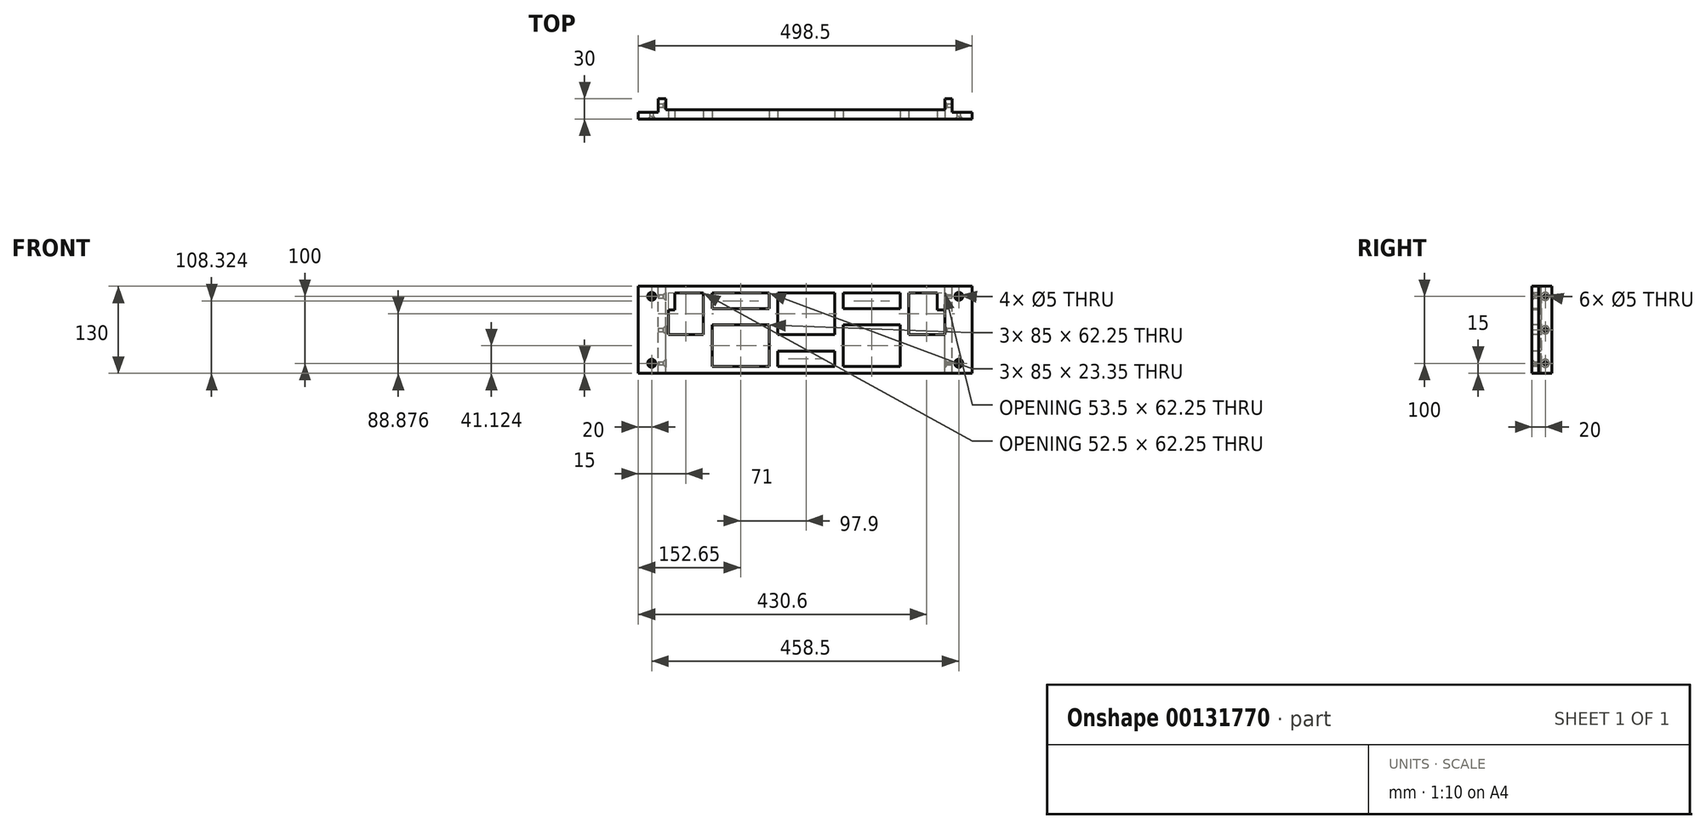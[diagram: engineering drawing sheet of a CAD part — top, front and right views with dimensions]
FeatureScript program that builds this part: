
annotation { "Feature Type Name" : "Feature", "Feature Type Description" : "" }
export const myFeature = defineFeature(function(context is Context, id is Id, definition is map)
    precondition{}
    {
        {
            var Q0;
            Q0=qCreatedBy(makeId("Front.planeOp"),FACE);
            var sketch = newSketch(context, id + "F0", { "sketchPlane" : qUnion([Q0])});
            skLineSegment(sketch, "E0.bottom", {"start": v(0, 0) * mm, "end": v(438.5, 0) * mm});
            skLineSegment(sketch, "E0.top", {"start": v(0, 130) * mm, "end": v(438.5, 130) * mm});
            skLineSegment(sketch, "E0.left", {"start": v(0, 0) * mm, "end": v(0, 130) * mm});
            skLineSegment(sketch, "E0.right", {"start": v(438.5, 0) * mm, "end": v(438.5, 130) * mm});
            skSolve(sketch);
        }
        {
            var Q0;
            Q0=makeQuery(id+"F0.imprint","IMPRINT",FACE,{"disambiguationData":[TD([[makeQuery(id+"F0.imprint","IMPRINT",EDGE,{"derivedFrom":sQuery(id+"F0.wireOp",EDGE,"E0.bottom")}),1.0]])]});
            extrude(context, id + "F1", {"entities" : qUnion([Q0]), "depth" : 14 * mm});
        }
        {
            var Q0;
            Q0=makeQuery(id+"F1.opExtrude","SWEPT_FACE",FACE,{"disambiguationData":[OSD([sQuery(id+"F0.wireOp",EDGE,"E0.top")])]});
            var sketch = newSketch(context, id + "F2", { "sketchPlane" : qUnion([Q0])});
            skLineSegment(sketch, "E1", {"start": v(0, -14) * mm, "end": v(-30, -14) * mm});
            skLineSegment(sketch, "E2", {"start": v(-30, -14) * mm, "end": v(-30, -4) * mm});
            skLineSegment(sketch, "E3", {"start": v(-30, -4) * mm, "end": v(0, -4) * mm});
            skLineSegment(sketch, "E4", {"start": v(0, -4) * mm, "end": v(0, -14) * mm});
            skLineSegment(sketch, "E5.bottom", {"start": v(438.5, -14) * mm, "end": v(468.5, -14) * mm});
            skLineSegment(sketch, "E5.top", {"start": v(438.5, -4) * mm, "end": v(468.5, -4) * mm});
            skLineSegment(sketch, "E5.left", {"start": v(438.5, -14) * mm, "end": v(438.5, -4) * mm});
            skLineSegment(sketch, "E6", {"start": v(468.5, -4) * mm, "end": v(468.5, -14) * mm});
            skSolve(sketch);
        }
        {
            var Q0;
            Q0=makeQuery(id+"F2.imprint","IMPRINT",FACE,{"disambiguationData":[TD([[makeQuery(id+"F2.imprint","IMPRINT",EDGE,{"derivedFrom":sQuery(id+"F2.wireOp",EDGE,"E5.bottom")}),1.0]])]});
            var Q1;
            Q1=makeQuery(id+"F2.imprint","IMPRINT",FACE,{"disambiguationData":[TD([[makeQuery(id+"F2.imprint","IMPRINT",EDGE,{"derivedFrom":sQuery(id+"F2.wireOp",EDGE,"E1")}),-1.0]])]});
            var Q2;
            Q2=makeQuery(id+"F2.imprint","IMPRINT",FACE,{"disambiguationData":[TD([[makeQuery(id+"F2.imprint","IMPRINT",EDGE,{"derivedFrom":sQuery(id+"F2.wireOp",EDGE,"RW2Kzl6v-dZsG-AqaK-MO7M-Wq128sQEg4HD.bottom")}),-1.0]])]});
            var Q3;
            Q3=makeQuery(id+"F1.opExtrude","SWEPT_FACE",FACE,{"disambiguationData":[OSD([sQuery(id+"F0.wireOp",EDGE,"E0.bottom")])]});
            extrude(context, id + "F3", {"entities" : qUnion([Q0, Q1, Q2]), "operationType" : NewBodyOperationType.ADD, "endBound" : BoundingType.UP_TO_SURFACE, "oppositeDirection" : true, "endBoundEntityFace" : qUnion([Q3]), "depth" : 25 * mm});
        }
        {
            var Q0;
            Q0=makeQuery(id+"F3.boolean.opBoolean","MERGE",FACE,{"derivedFrom":[makeQuery(id+"F1.opExtrude","SWEPT_FACE",FACE,{"disambiguationData":[OSD([sQuery(id+"F0.wireOp",EDGE,"E0.top")])]}),makeQuery(id+"F3.opExtrude","CAP_FACE",FACE,{"disambiguationData":[OSD([sQuery(id+"F2.wireOp",EDGE,"E1"),sQuery(id+"F2.wireOp",EDGE,"E2"),sQuery(id+"F2.wireOp",EDGE,"E3"),sQuery(id+"F2.wireOp",EDGE,"E4")])],"isStart":true}),makeQuery(id+"F3.opExtrude","CAP_FACE",FACE,{"disambiguationData":[OSD([sQuery(id+"F2.wireOp",EDGE,"E5.bottom"),sQuery(id+"F2.wireOp",EDGE,"E5.top"),sQuery(id+"F2.wireOp",EDGE,"E5.left"),sQuery(id+"F2.wireOp",EDGE,"E5.right")])],"isStart":true})]});
            var sketch = newSketch(context, id + "F4", { "sketchPlane" : qUnion([Q0])});
            skLineSegment(sketch, "E7", {"start": v(0, 0) * mm, "end": v(0, 16) * mm});
            skLineSegment(sketch, "E8", {"start": v(0, 16) * mm, "end": v(11, 16) * mm});
            skLineSegment(sketch, "E9", {"start": v(11, 16) * mm, "end": v(11, 0) * mm});
            skLineSegment(sketch, "E10", {"start": v(11, 0) * mm, "end": v(0, 0) * mm});
            skLineSegment(sketch, "E11.bottom", {"start": v(438.5, 0) * mm, "end": v(427.5, 0) * mm});
            skLineSegment(sketch, "E11.top", {"start": v(438.5, 16) * mm, "end": v(427.5, 16) * mm});
            skLineSegment(sketch, "E11.left", {"start": v(438.5, 0) * mm, "end": v(438.5, 16) * mm});
            skLineSegment(sketch, "E11.right", {"start": v(427.5, 0) * mm, "end": v(427.5, 16) * mm});
            skSolve(sketch);
        }
        {
            var Q0;
            Q0=makeQuery(id+"F4.imprint","IMPRINT",FACE,{"disambiguationData":[TD([[makeQuery(id+"F4.imprint","IMPRINT",EDGE,{"derivedFrom":sQuery(id+"F4.wireOp",EDGE,"g1681GE8-kr8q-vAWY-LNZA-GesWc0OhcODc.bottom")}),1.0]])]});
            var Q1;
            Q1=makeQuery(id+"F4.imprint","IMPRINT",FACE,{"disambiguationData":[TD([[makeQuery(id+"F4.imprint","IMPRINT",EDGE,{"derivedFrom":sQuery(id+"F4.wireOp",EDGE,"E7")}),-1.0]])]});
            var Q2;
            Q2=makeQuery(id+"F4.imprint","IMPRINT",FACE,{"disambiguationData":[TD([[makeQuery(id+"F4.imprint","IMPRINT",EDGE,{"derivedFrom":sQuery(id+"F4.wireOp",EDGE,"E11.bottom")}),1.0]])]});
            var Q3;
            {var subQ0=sQuery(id+"F0.wireOp",EDGE,"E0.bottom");Q3=makeQuery(id+"F3.boolean.opBoolean","MERGE",FACE,{"derivedFrom":[makeQuery(id+"F1.opExtrude","SWEPT_FACE",FACE,{"disambiguationData":[OSD([subQ0])]}),makeQuery(id+"F3.opExtrude","CAP_FACE",FACE,{"disambiguationData":[OSD([subQ0]),ownerDisambiguation([makeQuery(id+"F3.opExtrude","SWEPT_BODY",BODY,{"disambiguationData":[OSD([sQuery(id+"F2.wireOp",EDGE,"E1"),sQuery(id+"F2.wireOp",EDGE,"E2"),sQuery(id+"F2.wireOp",EDGE,"E3"),sQuery(id+"F2.wireOp",EDGE,"E4")])]})])],"isStart":false}),makeQuery(id+"F3.opExtrude","CAP_FACE",FACE,{"disambiguationData":[OSD([subQ0]),ownerDisambiguation([makeQuery(id+"F3.opExtrude","SWEPT_BODY",BODY,{"disambiguationData":[OSD([sQuery(id+"F2.wireOp",EDGE,"E5.bottom"),sQuery(id+"F2.wireOp",EDGE,"E5.top"),sQuery(id+"F2.wireOp",EDGE,"E5.left"),sQuery(id+"F2.wireOp",EDGE,"E5.right")])]})])],"isStart":false})]});}
            extrude(context, id + "F5", {"entities" : qUnion([Q0, Q1, Q2]), "operationType" : NewBodyOperationType.ADD, "endBound" : BoundingType.UP_TO_SURFACE, "oppositeDirection" : true, "endBoundEntityFace" : qUnion([Q3]), "depth" : 25 * mm});
        }
        {
            var Q0;
            Q0=makeQuery(id+"F3.boolean.opBoolean","MERGE",FACE,{"derivedFrom":[makeQuery(id+"F1.opExtrude","CAP_FACE",FACE,{"disambiguationData":[OSD([sQuery(id+"F0.wireOp",EDGE,"E0.bottom"),sQuery(id+"F0.wireOp",EDGE,"E0.top"),sQuery(id+"F0.wireOp",EDGE,"E0.left"),sQuery(id+"F0.wireOp",EDGE,"E0.right")])],"isStart":false}),makeQuery(id+"F3.opExtrude","SWEPT_FACE",FACE,{"disambiguationData":[OSD([sQuery(id+"F2.wireOp",EDGE,"E1")])]}),makeQuery(id+"F3.opExtrude","SWEPT_FACE",FACE,{"disambiguationData":[OSD([sQuery(id+"F2.wireOp",EDGE,"E5.bottom")])]})]});
            var sketch = newSketch(context, id + "F6", { "sketchPlane" : qUnion([Q0])});
            skLineSegment(sketch, "E12.0", {"start": v(24.75, 95) * mm, "end": v(24.75, 120) * mm});
            skLineSegment(sketch, "E12.2", {"start": v(427.35, 95) * mm, "end": v(427.35, 57.75) * mm});
            skLineSegment(sketch, "E12.3", {"start": v(416.35, 95) * mm, "end": v(427.35, 95) * mm});
            skLineSegment(sketch, "E12.4", {"start": v(416.35, 95) * mm, "end": v(416.35, 120) * mm});
            skLineSegment(sketch, "E12.5", {"start": v(416.35, 10) * mm, "end": v(416.35, 33.35) * mm});
            skLineSegment(sketch, "E12.6", {"start": v(24.75, 120) * mm, "end": v(416.35, 120) * mm});
            skLineSegment(sketch, "E12.7", {"start": v(416.35, 10) * mm, "end": v(24.75, 10) * mm});
            skLineSegment(sketch, "E12.8", {"start": v(24.75, 10) * mm, "end": v(24.75, 33.35) * mm});
            skLineSegment(sketch, "E12.11", {"start": v(14.75, 95) * mm, "end": v(24.75, 95) * mm});
            skLineSegment(sketch, "E13", {"start": v(122.65, 120) * mm, "end": v(122.65, 10) * mm});
            skLineSegment(sketch, "E14", {"start": v(220.55, 120) * mm, "end": v(220.55, 10) * mm});
            skLineSegment(sketch, "E15", {"start": v(318.45, 120) * mm, "end": v(318.45, 10) * mm});
            skLineSegment(sketch, "E16", {"start": v(24.75, 10) * mm, "end": v(122.65, 120) * mm, "construction": true});
            skLineSegment(sketch, "E17", {"start": v(122.65, 120) * mm, "end": v(220.55, 10) * mm, "construction": true});
            skLineSegment(sketch, "E18", {"start": v(220.55, 10) * mm, "end": v(318.45, 120) * mm, "construction": true});
            skLineSegment(sketch, "E19", {"start": v(318.45, 120) * mm, "end": v(416.35, 10) * mm, "construction": true});
            skLineSegment(sketch, "E20.bottom", {"start": v(80.15, 72.25) * mm, "end": v(165.15, 72.25) * mm});
            skLineSegment(sketch, "E20.top", {"start": v(80.15, 10) * mm, "end": v(165.15, 10) * mm});
            skLineSegment(sketch, "E20.left", {"start": v(80.15, 72.25) * mm, "end": v(80.15, 10) * mm});
            skLineSegment(sketch, "E20.right", {"start": v(165.15, 72.25) * mm, "end": v(165.15, 10) * mm});
            skLineSegment(sketch, "E21.bottom", {"start": v(263.05, 57.75) * mm, "end": v(178.05, 57.75) * mm});
            skLineSegment(sketch, "E21.top", {"start": v(263.05, 120) * mm, "end": v(178.05, 120) * mm});
            skLineSegment(sketch, "E21.left", {"start": v(263.05, 57.75) * mm, "end": v(263.05, 120) * mm});
            skLineSegment(sketch, "E21.right", {"start": v(178.05, 57.75) * mm, "end": v(178.05, 120) * mm});
            skLineSegment(sketch, "E22.bottom", {"start": v(275.95, 72.25) * mm, "end": v(360.95, 72.25) * mm});
            skLineSegment(sketch, "E22.top", {"start": v(275.95, 10) * mm, "end": v(360.95, 10) * mm});
            skLineSegment(sketch, "E22.left", {"start": v(275.95, 72.25) * mm, "end": v(275.95, 10) * mm});
            skLineSegment(sketch, "E22.right", {"start": v(360.95, 72.25) * mm, "end": v(360.95, 10) * mm});
            skLineSegment(sketch, "E23.bottom", {"start": v(67.25, 120) * mm, "end": v(24.75, 120) * mm});
            skLineSegment(sketch, "E23.top", {"start": v(67.25, 57.75) * mm, "end": v(24.75, 57.75) * mm});
            skLineSegment(sketch, "E23.left", {"start": v(67.25, 120) * mm, "end": v(67.25, 57.75) * mm});
            skLineSegment(sketch, "E23.right", {"start": v(24.75, 120) * mm, "end": v(24.75, 95) * mm});
            skLineSegment(sketch, "E24.bottom", {"start": v(416.35, 120) * mm, "end": v(373.85, 120) * mm});
            skLineSegment(sketch, "E24.top", {"start": v(427.35, 57.75) * mm, "end": v(373.85, 57.75) * mm});
            skLineSegment(sketch, "E24.left", {"start": v(416.35, 120) * mm, "end": v(416.35, 95) * mm});
            skLineSegment(sketch, "E24.right", {"start": v(373.85, 120) * mm, "end": v(373.85, 57.75) * mm});
            skLineSegment(sketch, "E25", {"start": v(24.75, 57.75) * mm, "end": v(14.75, 57.75) * mm});
            skLineSegment(sketch, "E26.bottom", {"start": v(80.15, 120) * mm, "end": v(165.15, 120) * mm});
            skLineSegment(sketch, "E26.top", {"start": v(80.15, 96.65) * mm, "end": v(165.15, 96.65) * mm});
            skLineSegment(sketch, "E26.left", {"start": v(80.15, 120) * mm, "end": v(80.15, 96.65) * mm});
            skLineSegment(sketch, "E26.right", {"start": v(165.15, 120) * mm, "end": v(165.15, 96.65) * mm});
            skLineSegment(sketch, "E27.bottom", {"start": v(178.05, 10) * mm, "end": v(263.05, 10) * mm});
            skLineSegment(sketch, "E27.top", {"start": v(178.05, 33.35) * mm, "end": v(263.05, 33.35) * mm});
            skLineSegment(sketch, "E27.left", {"start": v(178.05, 10) * mm, "end": v(178.05, 33.35) * mm});
            skLineSegment(sketch, "E27.right", {"start": v(263.05, 10) * mm, "end": v(263.05, 33.35) * mm});
            skLineSegment(sketch, "E28.bottom", {"start": v(275.95, 120) * mm, "end": v(360.95, 120) * mm});
            skLineSegment(sketch, "E28.top", {"start": v(275.95, 96.65) * mm, "end": v(360.95, 96.65) * mm});
            skLineSegment(sketch, "E28.left", {"start": v(275.95, 120) * mm, "end": v(275.95, 96.65) * mm});
            skLineSegment(sketch, "E28.right", {"start": v(360.95, 120) * mm, "end": v(360.95, 96.65) * mm});
            skLineSegment(sketch, "E29.bottom", {"start": v(24.75, 10) * mm, "end": v(67.25, 10) * mm});
            skLineSegment(sketch, "E29.top", {"start": v(24.75, 33.35) * mm, "end": v(67.25, 33.35) * mm});
            skLineSegment(sketch, "E29.right", {"start": v(67.25, 10) * mm, "end": v(67.25, 33.35) * mm});
            skLineSegment(sketch, "E30.bottom", {"start": v(416.35, 10) * mm, "end": v(373.85, 10) * mm});
            skLineSegment(sketch, "E30.top", {"start": v(416.35, 33.35) * mm, "end": v(373.85, 33.35) * mm});
            skLineSegment(sketch, "E30.right", {"start": v(373.85, 10) * mm, "end": v(373.85, 33.35) * mm});
            skLineSegment(sketch, "E31", {"start": v(14.75, 95) * mm, "end": v(14.75, 57.75) * mm});
            skSolve(sketch);
        }
        {
            var Q0;
            {var subQ0=sQuery(id+"F6.wireOp",EDGE,"E12.11");Q0=makeQuery(id+"F6.imprint","IMPRINT",FACE,{"disambiguationData":[TD([[makeQuery(id+"F6.imprint","IMPRINT",EDGE,{"derivedFrom":subQ0}),-1.0]])]});}
            var Q1;
            Q1=makeQuery(id+"F6.imprint","IMPRINT",FACE,{"disambiguationData":[TD([[makeQuery(id+"F6.imprint","IMPRINT",EDGE,{"derivedFrom":sQuery(id+"F6.wireOp",EDGE,"E29.bottom")}),1.0]])]});
            var Q2;
            {var subQ5=sQuery(id+"F6.wireOp",EDGE,"E20.left");Q2=makeQuery(id+"F6.imprint","IMPRINT",FACE,{"disambiguationData":[TD([[makeQuery(id+"F6.imprint","IMPRINT",EDGE,{"derivedFrom":subQ5}),1.0]])]});}
            var Q3;
            {var subQ5=sQuery(id+"F6.wireOp",EDGE,"E20.right");Q3=makeQuery(id+"F6.imprint","IMPRINT",FACE,{"disambiguationData":[TD([[makeQuery(id+"F6.imprint","IMPRINT",EDGE,{"derivedFrom":subQ5}),-1.0]])]});}
            var Q4;
            {var subQ5=sQuery(id+"F6.wireOp",EDGE,"E26.left");Q4=makeQuery(id+"F6.imprint","IMPRINT",FACE,{"disambiguationData":[TD([[makeQuery(id+"F6.imprint","IMPRINT",EDGE,{"derivedFrom":subQ5}),1.0]])]});}
            var Q5;
            {var subQ5=sQuery(id+"F6.wireOp",EDGE,"E26.right");Q5=makeQuery(id+"F6.imprint","IMPRINT",FACE,{"disambiguationData":[TD([[makeQuery(id+"F6.imprint","IMPRINT",EDGE,{"derivedFrom":subQ5}),-1.0]])]});}
            var Q6;
            {var subQ5=sQuery(id+"F6.wireOp",EDGE,"E21.right");Q6=makeQuery(id+"F6.imprint","IMPRINT",FACE,{"disambiguationData":[TD([[makeQuery(id+"F6.imprint","IMPRINT",EDGE,{"derivedFrom":subQ5}),-1.0]])]});}
            var Q7;
            {var subQ5=sQuery(id+"F6.wireOp",EDGE,"E21.left");Q7=makeQuery(id+"F6.imprint","IMPRINT",FACE,{"disambiguationData":[TD([[makeQuery(id+"F6.imprint","IMPRINT",EDGE,{"derivedFrom":subQ5}),1.0]])]});}
            var Q8;
            {var subQ5=sQuery(id+"F6.wireOp",EDGE,"E27.left");Q8=makeQuery(id+"F6.imprint","IMPRINT",FACE,{"disambiguationData":[TD([[makeQuery(id+"F6.imprint","IMPRINT",EDGE,{"derivedFrom":subQ5}),-1.0]])]});}
            var Q9;
            {var subQ5=sQuery(id+"F6.wireOp",EDGE,"E27.right");Q9=makeQuery(id+"F6.imprint","IMPRINT",FACE,{"disambiguationData":[TD([[makeQuery(id+"F6.imprint","IMPRINT",EDGE,{"derivedFrom":subQ5}),1.0]])]});}
            var Q10;
            {var subQ5=sQuery(id+"F6.wireOp",EDGE,"E22.left");Q10=makeQuery(id+"F6.imprint","IMPRINT",FACE,{"disambiguationData":[TD([[makeQuery(id+"F6.imprint","IMPRINT",EDGE,{"derivedFrom":subQ5}),1.0]])]});}
            var Q11;
            {var subQ5=sQuery(id+"F6.wireOp",EDGE,"E22.right");Q11=makeQuery(id+"F6.imprint","IMPRINT",FACE,{"disambiguationData":[TD([[makeQuery(id+"F6.imprint","IMPRINT",EDGE,{"derivedFrom":subQ5}),-1.0]])]});}
            var Q12;
            {var subQ5=sQuery(id+"F6.wireOp",EDGE,"E28.right");Q12=makeQuery(id+"F6.imprint","IMPRINT",FACE,{"disambiguationData":[TD([[makeQuery(id+"F6.imprint","IMPRINT",EDGE,{"derivedFrom":subQ5}),-1.0]])]});}
            var Q13;
            {var subQ5=sQuery(id+"F6.wireOp",EDGE,"E28.left");Q13=makeQuery(id+"F6.imprint","IMPRINT",FACE,{"disambiguationData":[TD([[makeQuery(id+"F6.imprint","IMPRINT",EDGE,{"derivedFrom":subQ5}),1.0]])]});}
            var Q14;
            {var subQ0=sQuery(id+"F6.wireOp",EDGE,"E12.3");Q14=makeQuery(id+"F6.imprint","IMPRINT",FACE,{"disambiguationData":[TD([[makeQuery(id+"F6.imprint","IMPRINT",EDGE,{"derivedFrom":subQ0}),-1.0]])]});}
            var Q15;
            Q15=makeQuery(id+"F6.imprint","IMPRINT",FACE,{"disambiguationData":[TD([[makeQuery(id+"F6.imprint","IMPRINT",EDGE,{"derivedFrom":sQuery(id+"F6.wireOp",EDGE,"E30.bottom")}),-1.0]])]});
            extrude(context, id + "F7", {"entities" : qUnion([Q0, Q1, Q2, Q3, Q4, Q5, Q6, Q7, Q8, Q9, Q10, Q11, Q12, Q13, Q14, Q15]), "operationType" : NewBodyOperationType.REMOVE, "oppositeDirection" : true, "depth" : 25 * mm});
        }
        {
            var Q0;
            Q0=makeQuery(id+"F3.opExtrude","SWEPT_FACE",FACE,{"disambiguationData":[OSD([sQuery(id+"F2.wireOp",EDGE,"E5.top")])]});
            var sketch = newSketch(context, id + "F8", { "sketchPlane" : qUnion([Q0])});
            skCircle(sketch, "E32", {"center": v(-448.5, 115) * mm, "radius": 2.5 * mm});
            skCircle(sketch, "E33", {"center": v(-448.5, 15) * mm, "radius": 2.5 * mm});
            skCircle(sketch, "E34", {"center": v(10, 115) * mm, "radius": 2.5 * mm});
            skCircle(sketch, "E35", {"center": v(10, 15) * mm, "radius": 2.5 * mm});
            skLineSegment(sketch, "E36.bottom", {"start": v(-448.5, 115) * mm, "end": v(10, 115) * mm, "construction": true});
            skLineSegment(sketch, "E36.top", {"start": v(-448.5, 15) * mm, "end": v(10, 15) * mm, "construction": true});
            skLineSegment(sketch, "E36.left", {"start": v(-448.5, 115) * mm, "end": v(-448.5, 15) * mm, "construction": true});
            skLineSegment(sketch, "E36.right", {"start": v(10, 115) * mm, "end": v(10, 15) * mm, "construction": true});
            skSolve(sketch);
        }
        {
            var Q0;
            Q0 = qSketchRegion(id + "F8", true);
            extrude(context, id + "F9", {"entities" : qUnion([Q0]), "operationType" : NewBodyOperationType.REMOVE, "oppositeDirection" : true, "depth" : 25 * mm});
        }
        {
            var Q0;
            Q0=makeQuery(id+"F5.boolean.opBoolean","MERGE",FACE,{"derivedFrom":[makeQuery(id+"F1.opExtrude","SWEPT_FACE",FACE,{"disambiguationData":[OSD([sQuery(id+"F0.wireOp",EDGE,"E0.right")])]}),makeQuery(id+"F5.opExtrude","SWEPT_FACE",FACE,{"disambiguationData":[OSD([sQuery(id+"F4.wireOp",EDGE,"E11.left")])]})]});
            var sketch = newSketch(context, id + "F10", { "sketchPlane" : qUnion([Q0])});
            skCircle(sketch, "E37", {"center": v(6, 115) * mm, "radius": 2.5 * mm});
            skCircle(sketch, "E38", {"center": v(6, 15) * mm, "radius": 2.5 * mm});
            skCircle(sketch, "E39", {"center": v(6, 65) * mm, "radius": 2.5 * mm});
            skSolve(sketch);
        }
        {
            var Q0;
            Q0 = qSketchRegion(id + "F10", true);
            extrude(context, id + "F11", {"entities" : qUnion([Q0]), "operationType" : NewBodyOperationType.REMOVE, "endBound" : BoundingType.THROUGH_ALL, "oppositeDirection" : true, "depth" : 25 * mm});
        }
        {
            var Q0;
            Q0=makeQuery(id+"F9.boolean.opBoolean","INTERSECT",EDGE,{"derivedFrom":[makeQuery(id+"F3.boolean.opBoolean","MERGE",FACE,{"derivedFrom":[makeQuery(id+"F1.opExtrude","CAP_FACE",FACE,{"disambiguationData":[OSD([sQuery(id+"F0.wireOp",EDGE,"E0.bottom"),sQuery(id+"F0.wireOp",EDGE,"E0.top"),sQuery(id+"F0.wireOp",EDGE,"E0.left"),sQuery(id+"F0.wireOp",EDGE,"E0.right")])],"isStart":false}),makeQuery(id+"F3.opExtrude","SWEPT_FACE",FACE,{"disambiguationData":[OSD([sQuery(id+"F2.wireOp",EDGE,"E1")])]}),makeQuery(id+"F3.opExtrude","SWEPT_FACE",FACE,{"disambiguationData":[OSD([sQuery(id+"F2.wireOp",EDGE,"E5.bottom")])]})]}),makeQuery(id+"F9.opExtrude","SWEPT_FACE",FACE,{"disambiguationData":[OSD([sQuery(id+"F8.wireOp",EDGE,"E32")])]})]});
            var Q1;
            Q1=makeQuery(id+"F9.boolean.opBoolean","INTERSECT",EDGE,{"derivedFrom":[makeQuery(id+"F3.boolean.opBoolean","MERGE",FACE,{"derivedFrom":[makeQuery(id+"F1.opExtrude","CAP_FACE",FACE,{"disambiguationData":[OSD([sQuery(id+"F0.wireOp",EDGE,"E0.bottom"),sQuery(id+"F0.wireOp",EDGE,"E0.top"),sQuery(id+"F0.wireOp",EDGE,"E0.left"),sQuery(id+"F0.wireOp",EDGE,"E0.right")])],"isStart":false}),makeQuery(id+"F3.opExtrude","SWEPT_FACE",FACE,{"disambiguationData":[OSD([sQuery(id+"F2.wireOp",EDGE,"E1")])]}),makeQuery(id+"F3.opExtrude","SWEPT_FACE",FACE,{"disambiguationData":[OSD([sQuery(id+"F2.wireOp",EDGE,"E5.bottom")])]})]}),makeQuery(id+"F9.opExtrude","SWEPT_FACE",FACE,{"disambiguationData":[OSD([sQuery(id+"F8.wireOp",EDGE,"E33")])]})]});
            var Q2;
            Q2=makeQuery(id+"F9.boolean.opBoolean","INTERSECT",EDGE,{"derivedFrom":[makeQuery(id+"F3.boolean.opBoolean","MERGE",FACE,{"derivedFrom":[makeQuery(id+"F1.opExtrude","CAP_FACE",FACE,{"disambiguationData":[OSD([sQuery(id+"F0.wireOp",EDGE,"E0.bottom"),sQuery(id+"F0.wireOp",EDGE,"E0.top"),sQuery(id+"F0.wireOp",EDGE,"E0.left"),sQuery(id+"F0.wireOp",EDGE,"E0.right")])],"isStart":false}),makeQuery(id+"F3.opExtrude","SWEPT_FACE",FACE,{"disambiguationData":[OSD([sQuery(id+"F2.wireOp",EDGE,"E1")])]}),makeQuery(id+"F3.opExtrude","SWEPT_FACE",FACE,{"disambiguationData":[OSD([sQuery(id+"F2.wireOp",EDGE,"E5.bottom")])]})]}),makeQuery(id+"F9.opExtrude","SWEPT_FACE",FACE,{"disambiguationData":[OSD([sQuery(id+"F8.wireOp",EDGE,"E34")])]})]});
            var Q3;
            Q3=makeQuery(id+"F9.boolean.opBoolean","INTERSECT",EDGE,{"derivedFrom":[makeQuery(id+"F3.boolean.opBoolean","MERGE",FACE,{"derivedFrom":[makeQuery(id+"F1.opExtrude","CAP_FACE",FACE,{"disambiguationData":[OSD([sQuery(id+"F0.wireOp",EDGE,"E0.bottom"),sQuery(id+"F0.wireOp",EDGE,"E0.top"),sQuery(id+"F0.wireOp",EDGE,"E0.left"),sQuery(id+"F0.wireOp",EDGE,"E0.right")])],"isStart":false}),makeQuery(id+"F3.opExtrude","SWEPT_FACE",FACE,{"disambiguationData":[OSD([sQuery(id+"F2.wireOp",EDGE,"E1")])]}),makeQuery(id+"F3.opExtrude","SWEPT_FACE",FACE,{"disambiguationData":[OSD([sQuery(id+"F2.wireOp",EDGE,"E5.bottom")])]})]}),makeQuery(id+"F9.opExtrude","SWEPT_FACE",FACE,{"disambiguationData":[OSD([sQuery(id+"F8.wireOp",EDGE,"E35")])]})]});
            var Q4;
            Q4=makeQuery(id+"F11.boolean.opBoolean","INTERSECT",EDGE,{"derivedFrom":[makeQuery(id+"F5.opExtrude","SWEPT_FACE",FACE,{"disambiguationData":[OSD([sQuery(id+"F4.wireOp",EDGE,"E11.right")])]}),makeQuery(id+"F11.opExtrude","SWEPT_FACE",FACE,{"disambiguationData":[OSD([sQuery(id+"F10.wireOp",EDGE,"E37")])]})]});
            var Q5;
            Q5=makeQuery(id+"F11.boolean.opBoolean","INTERSECT",EDGE,{"derivedFrom":[makeQuery(id+"F5.opExtrude","SWEPT_FACE",FACE,{"disambiguationData":[OSD([sQuery(id+"F4.wireOp",EDGE,"E11.right")])]}),makeQuery(id+"F11.opExtrude","SWEPT_FACE",FACE,{"disambiguationData":[OSD([sQuery(id+"F10.wireOp",EDGE,"E39")])]})]});
            var Q6;
            Q6=makeQuery(id+"F11.boolean.opBoolean","INTERSECT",EDGE,{"derivedFrom":[makeQuery(id+"F5.opExtrude","SWEPT_FACE",FACE,{"disambiguationData":[OSD([sQuery(id+"F4.wireOp",EDGE,"E11.right")])]}),makeQuery(id+"F11.opExtrude","SWEPT_FACE",FACE,{"disambiguationData":[OSD([sQuery(id+"F10.wireOp",EDGE,"E38")])]})]});
            var Q7;
            Q7=makeQuery(id+"F11.boolean.opBoolean","INTERSECT",EDGE,{"derivedFrom":[makeQuery(id+"F5.opExtrude","SWEPT_FACE",FACE,{"disambiguationData":[OSD([sQuery(id+"F4.wireOp",EDGE,"E9")])]}),makeQuery(id+"F11.opExtrude","SWEPT_FACE",FACE,{"disambiguationData":[OSD([sQuery(id+"F10.wireOp",EDGE,"E37")])]})]});
            var Q8;
            Q8=makeQuery(id+"F11.boolean.opBoolean","INTERSECT",EDGE,{"derivedFrom":[makeQuery(id+"F5.opExtrude","SWEPT_FACE",FACE,{"disambiguationData":[OSD([sQuery(id+"F4.wireOp",EDGE,"E9")])]}),makeQuery(id+"F11.opExtrude","SWEPT_FACE",FACE,{"disambiguationData":[OSD([sQuery(id+"F10.wireOp",EDGE,"E39")])]})]});
            var Q9;
            Q9=makeQuery(id+"F11.boolean.opBoolean","INTERSECT",EDGE,{"derivedFrom":[makeQuery(id+"F5.opExtrude","SWEPT_FACE",FACE,{"disambiguationData":[OSD([sQuery(id+"F4.wireOp",EDGE,"E9")])]}),makeQuery(id+"F11.opExtrude","SWEPT_FACE",FACE,{"disambiguationData":[OSD([sQuery(id+"F10.wireOp",EDGE,"E38")])]})]});
            chamfer(context, id + "F12", {"entities" : qUnion([Q0, Q1, Q2, Q3, Q4, Q5, Q6, Q7, Q8, Q9]), "width" : 3.5 * mm, "tangentPropagation" : true});
        }
    });
